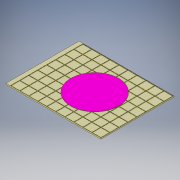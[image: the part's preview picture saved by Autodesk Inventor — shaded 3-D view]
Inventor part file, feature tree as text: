
AUTODESK INVENTOR PART (.ipt)
format: ipt  version: 2019 (Build 230136000, 136)  size: 421,376 bytes
history: native  units: mm
features: extrude x3, sketch x3, pattern_linear x1, plane x1
ambient origin geometry x8: Origin, YZ Plane, XZ Plane, XY Plane, X Axis, Y Axis, Z Axis, Center Point
bodies: Solid1 (feature_tree)
feature tree (8):
  extrude  "Extrusion1"  Depth=77.0mm
  extrude  "Extrusion2"  Depth=10.0mm
  pattern_linear  "Rectangular Pattern1"  Spacing1=0.5mm  [1 undecoded]
  plane  "Work Plane1"
  extrude  "Extrusion4"  Depth=0.15mm TaperAngle=0.0deg
  sketch  "Sketch1"  dims[d0=100.0mm d1=77.0mm]
  sketch  "Sketch2"  dims[d2=1.0mm d3=0.0mm d4=10.0mm]
  sketch  "Sketch4"  dims[d5=10.0mm d6=0.5mm d7=0.15mm d8=0.0mm d9=100.0mm d11=9.5mm d12=80.0mm d14=9.5mm d20=0.0mm d21=50.4mm d22=45.0mm d23=38.5mm d24=0.3mm d25=0.0mm]
note: 1 required parameter value undecoded (feature->parameter linkage not recoverable at this tier; creation-order binding heuristic only, values carry confidence <= 0.55)
